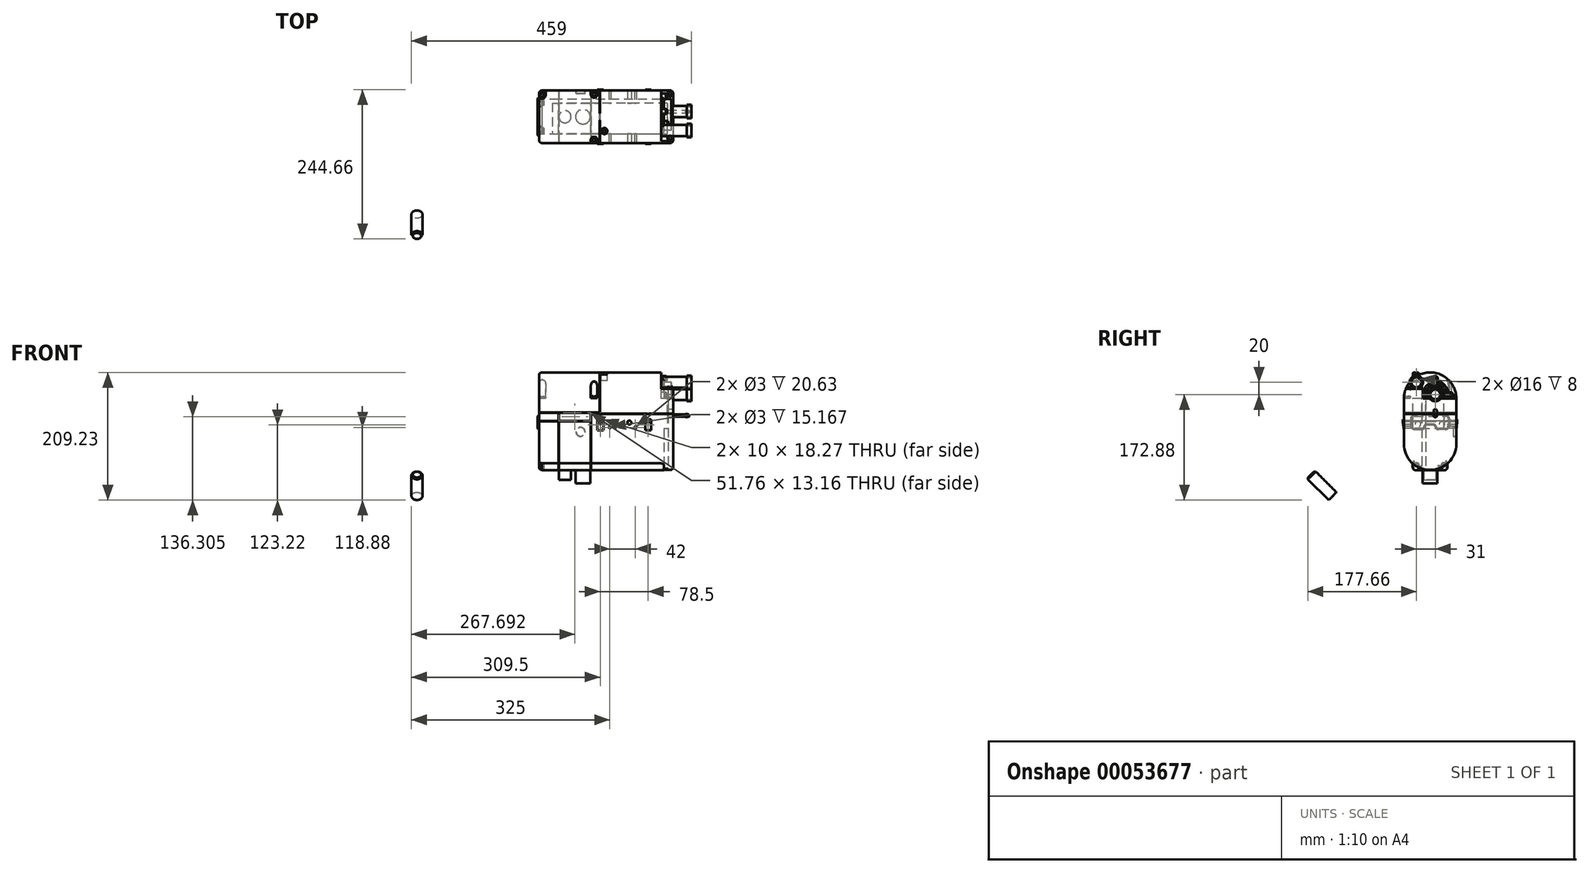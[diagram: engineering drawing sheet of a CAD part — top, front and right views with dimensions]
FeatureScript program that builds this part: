
annotation { "Feature Type Name" : "Feature", "Feature Type Description" : "" }
export const myFeature = defineFeature(function(context is Context, id is Id, definition is map)
    precondition{}
    {
        {
            var Q0;
            Q0=qCreatedBy(makeId("Front.planeOp"),FACE);
            var sketch = newSketch(context, id + "F0", { "sketchPlane" : qUnion([Q0])});
            skLineSegment(sketch, "E0.bottom", {"start": v(0, 160) * mm, "end": v(220, 160) * mm});
            skLineSegment(sketch, "E0.top", {"start": v(0, 0) * mm, "end": v(220, 0) * mm});
            skLineSegment(sketch, "E0.left", {"start": v(0, 160) * mm, "end": v(0, 0) * mm});
            skLineSegment(sketch, "E0.right", {"start": v(220, 160) * mm, "end": v(220, 0) * mm});
            skLineSegment(sketch, "E1", {"start": v(220, 144) * mm, "end": v(255.31, 144) * mm, "construction": true});
            skLineSegment(sketch, "E2", {"start": v(220, 124) * mm, "end": v(252.52, 124) * mm, "construction": true});
            skLineSegment(sketch, "E3", {"start": v(199, 133.89) * mm, "end": v(199, 118.06) * mm});
            skLineSegment(sketch, "E4", {"start": v(236.23, 153) * mm, "end": v(236.23, 135) * mm, "construction": true});
            skLineSegment(sketch, "E5", {"start": v(123.03, 118) * mm, "end": v(43.7, 118) * mm});
            skLineSegment(sketch, "E6", {"start": v(5, 154.65) * mm, "end": v(5, 139.81) * mm});
            skLineSegment(sketch, "E7", {"start": v(205, 0) * mm, "end": v(205, 15.7) * mm});
            skLineSegment(sketch, "E8", {"start": v(43, 3.14) * mm, "end": v(43, -20.65) * mm});
            skLineSegment(sketch, "E9", {"start": v(72, 4.14) * mm, "end": v(72, -25) * mm});
            skLineSegment(sketch, "E10", {"start": v(33.26, -16) * mm, "end": v(52.94, -16) * mm});
            skLineSegment(sketch, "E11", {"start": v(59.34, -20) * mm, "end": v(83.9, -20) * mm});
            skLineSegment(sketch, "E12", {"start": v(220, 92.5) * mm, "end": v(85.03, 92.5) * mm});
            skLineSegment(sketch, "E13", {"start": v(246, 91.62) * mm, "end": v(246, 86.96) * mm});
            skLineSegment(sketch, "E14", {"start": v(217, 89) * mm, "end": v(251.41, 89) * mm});
            skLineSegment(sketch, "E15.bottom", {"start": v(243.5, 92.15) * mm, "end": v(240.5, 92.15) * mm});
            skLineSegment(sketch, "E15.top", {"start": v(243.5, 86.65) * mm, "end": v(240.5, 86.65) * mm});
            skLineSegment(sketch, "E15.left", {"start": v(243.5, 92.15) * mm, "end": v(243.5, 86.65) * mm});
            skLineSegment(sketch, "E15.right", {"start": v(240.5, 92.15) * mm, "end": v(240.5, 86.65) * mm});
            skLineSegment(sketch, "E16", {"start": v(101.2, 157) * mm, "end": v(111.86, 157) * mm});
            skLineSegment(sketch, "E17", {"start": v(-1.72, 87.54) * mm, "end": v(-1.72, 71.83) * mm});
            skLineSegment(sketch, "E18", {"start": v(206.56, 127.25) * mm, "end": v(206.56, 120.25) * mm});
            skLineSegment(sketch, "E19", {"start": v(206.56, 123.75) * mm, "end": v(208.56, 123.75) * mm});
            skLineSegment(sketch, "E20", {"start": v(89.7, 118) * mm, "end": v(89.7, 120.5) * mm});
            skSolve(sketch);
        }
        {
            var Q0;
            Q0=qCreatedBy(makeId("Right.planeOp"),FACE);
            var sketch = newSketch(context, id + "F1", { "sketchPlane" : qUnion([Q0])});
            skArc(sketch, "E21", {"start": v(86, 117.35) * mm, "mid": v(43, 160.35) * mm, "end": v(0, 117.35) * mm});
            skArc(sketch, "E22", {"start": v(0, 43.35) * mm, "mid": v(43, 0.35) * mm, "end": v(86, 43.35) * mm});
            skLineSegment(sketch, "E23", {"start": v(0, 117.35) * mm, "end": v(0, 43.35) * mm});
            skLineSegment(sketch, "E24", {"start": v(86, 117.35) * mm, "end": v(86, 43.35) * mm});
            skLineSegment(sketch, "E25", {"start": v(0, 83.29) * mm, "end": v(-2.3, 83.29) * mm, "construction": true});
            skLineSegment(sketch, "E26", {"start": v(86, 83.29) * mm, "end": v(87.7, 83.29) * mm, "construction": true});
            skSolve(sketch);
        }
        {
            var Q0;
            Q0=qCreatedBy(makeId("Top.planeOp"),FACE);
            var sketch = newSketch(context, id + "F2", { "sketchPlane" : qUnion([Q0])});
            skLineSegment(sketch, "E27", {"start": v(-0.36, 86) * mm, "end": v(219.64, 86) * mm});
            skLineSegment(sketch, "E28", {"start": v(-0.36, 0) * mm, "end": v(219.64, 0) * mm});
            skLineSegment(sketch, "E29", {"start": v(-0.36, 86) * mm, "end": v(-0.36, 0) * mm});
            skLineSegment(sketch, "E30", {"start": v(221.58, 20.5) * mm, "end": v(257.3, 20.5) * mm});
            skLineSegment(sketch, "E31", {"start": v(222.14, 51.5) * mm, "end": v(259.8, 51.5) * mm});
            skLineSegment(sketch, "E32", {"start": v(219.64, 86) * mm, "end": v(219.64, 0) * mm});
            skLineSegment(sketch, "E33", {"start": v(199.64, 81.83) * mm, "end": v(199.64, 54.29) * mm});
            skLineSegment(sketch, "E34", {"start": v(199.64, 75.94) * mm, "end": v(204.64, 75.94) * mm});
            skLineSegment(sketch, "E35", {"start": v(204.64, 75.94) * mm, "end": v(204.64, 27.94) * mm});
            skLineSegment(sketch, "E36", {"start": v(204.64, 27.94) * mm, "end": v(199.48, 27.94) * mm});
            skLineSegment(sketch, "E37", {"start": v(204.64, 74.7) * mm, "end": v(216.64, 74.7) * mm});
            skLineSegment(sketch, "E38", {"start": v(216.64, 74.7) * mm, "end": v(216.64, 29.7) * mm});
            skLineSegment(sketch, "E39", {"start": v(216.64, 29.7) * mm, "end": v(204.64, 29.7) * mm});
            skLineSegment(sketch, "E40", {"start": v(216.64, 67.02) * mm, "end": v(218.64, 67.02) * mm});
            skLineSegment(sketch, "E41", {"start": v(218.64, 67.02) * mm, "end": v(218.64, 34.02) * mm});
            skLineSegment(sketch, "E42", {"start": v(218.64, 34.02) * mm, "end": v(216.64, 34.02) * mm});
            skLineSegment(sketch, "E43", {"start": v(185.57, 86) * mm, "end": v(185.57, 87.56) * mm});
            skLineSegment(sketch, "E44", {"start": v(185.57, 87.56) * mm, "end": v(175.64, 87.56) * mm});
            skLineSegment(sketch, "E45", {"start": v(175.64, 87.56) * mm, "end": v(175.64, 86) * mm});
            skLineSegment(sketch, "E46", {"start": v(105.14, 86) * mm, "end": v(105.14, 87.5) * mm});
            skLineSegment(sketch, "E47", {"start": v(95.14, 86) * mm, "end": v(95.14, 87.5) * mm});
            skLineSegment(sketch, "E48", {"start": v(95.14, 87.5) * mm, "end": v(105.14, 87.5) * mm});
            skLineSegment(sketch, "E49", {"start": v(207.64, 74.7) * mm, "end": v(207.64, 82.59) * mm});
            skLineSegment(sketch, "E50", {"start": v(207.64, 82.59) * mm, "end": v(199.7, 82.59) * mm});
            skLineSegment(sketch, "E51", {"start": v(201.63, 54.6) * mm, "end": v(207.36, 54.6) * mm});
            skLineSegment(sketch, "E52", {"start": v(201.82, 46.6) * mm, "end": v(207.17, 46.6) * mm});
            skSolve(sketch);
        }
        {
            var Q0;
            Q0 = qSketchRegion(id + "F1", true);
            extrude(context, id + "F3", {"entities" : qUnion([Q0]), "depth" : 220 * mm});
        }
        {
            var Q0;
            Q0=makeQuery(id+"F3.opExtrude","CAP_FACE",FACE,{"disambiguationData":[OSD([sQuery(id+"F1.wireOp",EDGE,"E21"),sQuery(id+"F1.wireOp",EDGE,"E22"),sQuery(id+"F1.wireOp",EDGE,"E23"),sQuery(id+"F1.wireOp",EDGE,"E24")])],"isStart":false});
            var sketch = newSketch(context, id + "F4", { "sketchPlane" : qUnion([Q0])});
            skPoint(sketch, "E53.orphan", {"position": v(86, 117.35) * mm});
            skLineSegment(sketch, "E54", {"start": v(86, 117.35) * mm, "end": v(31.1, 117.35) * mm});
            skLineSegment(sketch, "E55", {"start": v(31.1, 117.35) * mm, "end": v(31.1, 133.35) * mm});
            skLineSegment(sketch, "E56", {"start": v(31.1, 133.35) * mm, "end": v(3.09, 133.35) * mm});
            skArc(sketch, "E57.0", {"start": v(86, 117.35) * mm, "mid": v(51.15, 159.57) * mm, "end": v(3.09, 133.35) * mm});
            skPoint(sketch, "E58.orphan", {"position": v(0, 117.35) * mm});
            skSolve(sketch);
        }
        {
            var Q0;
            Q0 = qSketchRegion(id + "F4", true);
            extrude(context, id + "F5", {"entities" : qUnion([Q0]), "operationType" : NewBodyOperationType.REMOVE, "oppositeDirection" : true, "depth" : 20 * mm});
        }
        {
            var Q0;
            Q0=makeQuery(id+"F5.boolean.opBoolean","COPY",FACE,{"derivedFrom":makeQuery(id+"F5.opExtrude","CAP_FACE",FACE,{"disambiguationData":[OSD([sQuery(id+"F4.wireOp",EDGE,"E54"),sQuery(id+"F4.wireOp",EDGE,"E55"),sQuery(id+"F4.wireOp",EDGE,"E56"),sQuery(id+"F4.wireOp",EDGE,"E57.0")])],"isStart":false})});
            var sketch = newSketch(context, id + "F6", { "sketchPlane" : qUnion([Q0])});
            skCircle(sketch, "E59", {"center": v(51.5, 124) * mm, "radius": 9 * mm});
            skCircle(sketch, "E60", {"center": v(20.5, 144) * mm, "radius": 9 * mm});
            skSolve(sketch);
        }
        {
            var Q0;
            Q0 = qSketchRegion(id + "F6", true);
            extrude(context, id + "F7", {"entities" : qUnion([Q0]), "operationType" : NewBodyOperationType.ADD, "depth" : 50 * mm});
        }
        {
            var Q0;
            Q0=makeQuery(id+"F7.opExtrude","CAP_FACE",FACE,{"disambiguationData":[OSD([sQuery(id+"F6.wireOp",EDGE,"E60")])],"isStart":false});
            var sketch = newSketch(context, id + "F8", { "sketchPlane" : qUnion([Q0])});
            skCircle(sketch, "E61", {"center": v(20.5, 144) * mm, "radius": 11 * mm});
            skCircle(sketch, "E62.0", {"center": v(51.5, 124) * mm, "radius": 9 * mm, "construction": true});
            skCircle(sketch, "E63", {"center": v(51.5, 124) * mm, "radius": 11 * mm});
            skCircle(sketch, "E64", {"center": v(20.5, 144) * mm, "radius": 8 * mm});
            skCircle(sketch, "E65", {"center": v(51.5, 124) * mm, "radius": 8 * mm});
            skSolve(sketch);
        }
        {
            var Q0;
            Q0 = qSketchRegion(id + "F8", true);
            extrude(context, id + "F9", {"entities" : qUnion([Q0]), "operationType" : NewBodyOperationType.ADD, "oppositeDirection" : true, "depth" : 8 * mm});
        }
        {
            var Q0;
            Q0=makeQuery(id+"F9.boolean.opBoolean","MERGE",FACE,{"derivedFrom":[makeQuery(id+"F7.opExtrude","CAP_FACE",FACE,{"disambiguationData":[OSD([sQuery(id+"F6.wireOp",EDGE,"E60")])],"isStart":false}),makeQuery(id+"F9.opExtrude","CAP_FACE",FACE,{"disambiguationData":[OSD([sQuery(id+"F8.wireOp",EDGE,"E61"),sQuery(id+"F8.wireOp",EDGE,"E64")])],"isStart":true})]});
            var sketch = newSketch(context, id + "F10", { "sketchPlane" : qUnion([Q0])});
            skCircle(sketch, "E66", {"center": v(20.5, 144) * mm, "radius": 8 * mm});
            skCircle(sketch, "E67.0", {"center": v(51.5, 124) * mm, "radius": 11 * mm, "construction": true});
            skCircle(sketch, "E68", {"center": v(51.5, 124) * mm, "radius": 8 * mm});
            skSolve(sketch);
        }
        {
            var Q0;
            Q0 = qSketchRegion(id + "F10", true);
            extrude(context, id + "F11", {"entities" : qUnion([Q0]), "operationType" : NewBodyOperationType.REMOVE, "oppositeDirection" : true, "depth" : 8 * mm});
        }
        {
            var Q0;
            Q0=makeQuery(id+"F5.boolean.opBoolean","COPY",FACE,{"derivedFrom":makeQuery(id+"F5.opExtrude","CAP_FACE",FACE,{"disambiguationData":[OSD([sQuery(id+"F4.wireOp",EDGE,"E54"),sQuery(id+"F4.wireOp",EDGE,"E55"),sQuery(id+"F4.wireOp",EDGE,"E56"),sQuery(id+"F4.wireOp",EDGE,"E57.0")])],"isStart":false})});
            var sketch = newSketch(context, id + "F12", { "sketchPlane" : qUnion([Q0])});
            skLineSegment(sketch, "E69", {"start": v(27.41, 149.76) * mm, "end": v(43, 149.76) * mm});
            skArc(sketch, "E70", {"start": v(43, 149.76) * mm, "mid": v(65.92, 140.27) * mm, "end": v(75.41, 117.35) * mm});
            skLineSegment(sketch, "E71.0", {"start": v(86, 117.35) * mm, "end": v(57.56, 117.35) * mm});
            skLineSegment(sketch, "E72.0", {"start": v(31.1, 117.35) * mm, "end": v(31.1, 133.35) * mm});
            skLineSegment(sketch, "E73.0", {"start": v(31.1, 133.35) * mm, "end": v(20.5, 133.35) * mm});
            skLineSegment(sketch, "E74", {"start": v(20.5, 144) * mm, "end": v(20.5, 133.35) * mm});
            skLineSegment(sketch, "E75", {"start": v(31.1, 117.35) * mm, "end": v(57.56, 117.35) * mm});
            skPoint(sketch, "E76.orphan", {"position": v(3.09, 133.35) * mm});
            skLineSegment(sketch, "E77", {"start": v(27.41, 149.76) * mm, "end": v(20.5, 144) * mm});
            skSolve(sketch);
        }
        {
            var Q0;
            {var subQ1=sQuery(id+"F12.wireOp",EDGE,"E69");Q0=makeQuery(id+"F12.imprint","IMPRINT",FACE,{"disambiguationData":[TD([[makeQuery(id+"F12.imprint","IMPRINT",EDGE,{"derivedFrom":subQ1}),-1.0]])]});}
            extrude(context, id + "F13", {"entities" : qUnion([Q0]), "operationType" : NewBodyOperationType.ADD, "depth" : 5 * mm});
        }
        {
            var Q0;
            Q0=makeQuery(id+"F13.opExtrude","CAP_FACE",FACE,{"disambiguationData":[OSD([sQuery(id+"F6.wireOp",EDGE,"E59"),sQuery(id+"F6.wireOp",EDGE,"E60"),sQuery(id+"F12.wireOp",EDGE,"E69"),sQuery(id+"F12.wireOp",EDGE,"E70"),sQuery(id+"F12.wireOp",EDGE,"E71.0"),sQuery(id+"F12.wireOp",EDGE,"E72.0"),sQuery(id+"F12.wireOp",EDGE,"E73.0"),sQuery(id+"F12.wireOp",EDGE,"E74"),sQuery(id+"F12.wireOp",EDGE,"E75")])],"isStart":false});
            var sketch = newSketch(context, id + "F14", { "sketchPlane" : qUnion([Q0])});
            skLineSegment(sketch, "E78", {"start": v(31.1, 117.35) * mm, "end": v(31.1, 124) * mm});
            skLineSegment(sketch, "E79", {"start": v(71.9, 117.35) * mm, "end": v(71.9, 124) * mm});
            skArc(sketch, "E80", {"start": v(71.9, 124) * mm, "mid": v(51.5, 144.4) * mm, "end": v(31.1, 124) * mm});
            skLineSegment(sketch, "E81", {"start": v(31.1, 117.35) * mm, "end": v(71.9, 117.35) * mm});
            skArc(sketch, "E82.0", {"start": v(20.5, 135) * mm, "mid": v(26.86, 137.64) * mm, "end": v(29.5, 144) * mm});
            skLineSegment(sketch, "E83", {"start": v(29.5, 144) * mm, "end": v(29.5, 133.35) * mm});
            skPoint(sketch, "E84.orphan", {"position": v(27.41, 149.76) * mm});
            skLineSegment(sketch, "E85", {"start": v(20.5, 133.35) * mm, "end": v(29.5, 133.35) * mm});
            skLineSegment(sketch, "E86", {"start": v(20.5, 135) * mm, "end": v(20.5, 133.35) * mm});
            skPoint(sketch, "E87.orphan", {"position": v(3.09, 133.35) * mm});
            skPoint(sketch, "E88.0.end.orphan", {"position": v(20.5, 135) * mm});
            skPoint(sketch, "E88.0.start.orphan", {"position": v(12.11, 147.26) * mm});
            skSolve(sketch);
        }
        {
            var Q0;
            Q0 = qSketchRegion(id + "F14", true);
            extrude(context, id + "F15", {"entities" : qUnion([Q0]), "operationType" : NewBodyOperationType.ADD, "depth" : 12 * mm});
        }
        {
            var Q0;
            Q0=makeQuery(id+"F15.opExtrude","CAP_FACE",FACE,{"disambiguationData":[OSD([sQuery(id+"F14.wireOp",EDGE,"E78"),sQuery(id+"F14.wireOp",EDGE,"E79"),sQuery(id+"F14.wireOp",EDGE,"E80"),sQuery(id+"F14.wireOp",EDGE,"E81")])],"isStart":false});
            var sketch = newSketch(context, id + "F16", { "sketchPlane" : qUnion([Q0])});
            skLineSegment(sketch, "E89", {"start": v(35, 117.35) * mm, "end": v(35, 124) * mm});
            skLineSegment(sketch, "E90", {"start": v(68, 117.35) * mm, "end": v(68, 124) * mm});
            skArc(sketch, "E91", {"start": v(68, 124) * mm, "mid": v(51.5, 140.5) * mm, "end": v(35, 124) * mm});
            skLineSegment(sketch, "E92", {"start": v(35, 117.35) * mm, "end": v(68, 117.35) * mm});
            skSolve(sketch);
        }
        {
            var Q0;
            Q0 = qSketchRegion(id + "F16", true);
            extrude(context, id + "F17", {"entities" : qUnion([Q0]), "operationType" : NewBodyOperationType.ADD, "depth" : 2 * mm});
        }
        {
            var Q0;
            Q0=qCreatedBy(makeId("Top.planeOp"),FACE);
            cPlane(context, id + "F18", {"entities" : qUnion([Q0]), "cplaneType" : CPlaneType.OFFSET, "offset" : 118 * mm, "width" : 150 * mm, "height" : 150 * mm});
        }
        {
            var Q0;
            Q0=qCreatedBy(id+"F18.planeOp",FACE);
            var sketch = newSketch(context, id + "F19", { "sketchPlane" : qUnion([Q0])});
            skLineSegment(sketch, "E93", {"start": v(0, 72.78) * mm, "end": v(5.07, 72.78) * mm});
            skLineSegment(sketch, "E94", {"start": v(10.79, 85.9) * mm, "end": v(10.79, 77.81) * mm});
            skLineSegment(sketch, "E95.0", {"start": v(-0.36, 86) * mm, "end": v(-0.36, 0) * mm, "construction": true});
            skLineSegment(sketch, "E95.1", {"start": v(-0.36, 86) * mm, "end": v(219.64, 86) * mm, "construction": true});
            skLineSegment(sketch, "E95.2", {"start": v(-0.36, 0) * mm, "end": v(219.64, 0) * mm, "construction": true});
            skLineSegment(sketch, "E96", {"start": v(84.87, 86) * mm, "end": v(84.87, 79.73) * mm});
            skLineSegment(sketch, "E97", {"start": v(95.62, 86) * mm, "end": v(95.62, 79.73) * mm});
            skLineSegment(sketch, "E98", {"start": v(84.82, 0) * mm, "end": v(84.82, 4.9) * mm});
            skLineSegment(sketch, "E99", {"start": v(95.57, 0) * mm, "end": v(95.57, 4.9) * mm});
            skArc(sketch, "E100", {"start": v(84.87, 79.73) * mm, "mid": v(90.25, 74.36) * mm, "end": v(95.62, 79.73) * mm});
            skArc(sketch, "E101", {"start": v(95.57, 4.9) * mm, "mid": v(90.2, 10.28) * mm, "end": v(84.82, 4.9) * mm});
            skArc(sketch, "E102", {"start": v(5.07, 72.78) * mm, "mid": v(8.88, 74.22) * mm, "end": v(10.79, 77.81) * mm});
            skLineSegment(sketch, "E103", {"start": v(0, 72.78) * mm, "end": v(-0.36, 86) * mm});
            skLineSegment(sketch, "E104", {"start": v(10.79, 85.9) * mm, "end": v(-0.36, 86) * mm, "construction": true});
            skLineSegment(sketch, "E105", {"start": v(84.87, 86) * mm, "end": v(95.62, 86) * mm});
            skLineSegment(sketch, "E106", {"start": v(84.82, 0) * mm, "end": v(95.57, 0) * mm});
            skLineSegment(sketch, "E107", {"start": v(10.79, 85.9) * mm, "end": v(10.79, 88.78) * mm});
            skLineSegment(sketch, "E108", {"start": v(10.79, 88.78) * mm, "end": v(-0.36, 88.78) * mm});
            skLineSegment(sketch, "E109", {"start": v(-0.36, 88.78) * mm, "end": v(-0.36, 86) * mm});
            skSolve(sketch);
        }
        {
            var Q0;
            Q0 = qSketchRegion(id + "F19", true);
            extrude(context, id + "F20", {"entities" : qUnion([Q0]), "operationType" : NewBodyOperationType.REMOVE, "endBound" : BoundingType.THROUGH_ALL, "depth" : 25 * mm});
        }
        {
            var Q0;
            Q0=makeQuery(id+"F17.opExtrude","CAP_EDGE",EDGE,{"disambiguationData":[OSD([sQuery(id+"F16.wireOp",EDGE,"E91")])],"isStart":false});
            chamfer(context, id + "F21", {"entities" : qUnion([Q0]), "width" : 2 * mm, "tangentPropagation" : true});
        }
        {
            var Q0;
            Q0=makeQuery(id+"F1.imprint","IMPRINT",FACE,{"disambiguationData":[TD([[makeQuery(id+"F1.imprint","IMPRINT",EDGE,{"derivedFrom":sQuery(id+"F1.wireOp",EDGE,"E21")}),1.0]])]});
            var sketch = newSketch(context, id + "F22", { "sketchPlane" : qUnion([Q0])});
            skArc(sketch, "E110.0", {"start": v(14.5, 11.15) * mm, "mid": v(43, 0.35) * mm, "end": v(71.5, 11.15) * mm});
            skLineSegment(sketch, "E111", {"start": v(71.5, 11.15) * mm, "end": v(71.5, 5) * mm});
            skArc(sketch, "E112", {"start": v(66.5, 0) * mm, "mid": v(70.04, 1.46) * mm, "end": v(71.5, 5) * mm});
            skLineSegment(sketch, "E113", {"start": v(66.5, 0) * mm, "end": v(19.5, 0) * mm});
            skLineSegment(sketch, "E114", {"start": v(14.5, 11.15) * mm, "end": v(14.5, 5) * mm});
            skArc(sketch, "E115", {"start": v(14.5, 5) * mm, "mid": v(15.96, 1.46) * mm, "end": v(19.5, 0) * mm});
            skPoint(sketch, "E116.orphan", {"position": v(86, 43.35) * mm});
            skPoint(sketch, "E117.orphan", {"position": v(0, 43.35) * mm});
            skSolve(sketch);
        }
        {
            var Q0;
            Q0 = qSketchRegion(id + "F22", true);
            extrude(context, id + "F23", {"entities" : qUnion([Q0]), "operationType" : NewBodyOperationType.ADD, "depth" : 205 * mm});
        }
        {
            var Q0;
            Q0=makeQuery(id+"F23.boolean.opBoolean","MERGE",FACE,{"derivedFrom":[makeQuery(id+"F3.opExtrude","CAP_FACE",FACE,{"disambiguationData":[OSD([sQuery(id+"F1.wireOp",EDGE,"E21"),sQuery(id+"F1.wireOp",EDGE,"E22"),sQuery(id+"F1.wireOp",EDGE,"E23"),sQuery(id+"F1.wireOp",EDGE,"E24")])],"isStart":true}),makeQuery(id+"F23.opExtrude","CAP_FACE",FACE,{"disambiguationData":[OSD([sQuery(id+"F22.wireOp",EDGE,"E110.0"),sQuery(id+"F22.wireOp",EDGE,"E111"),sQuery(id+"F22.wireOp",EDGE,"E112"),sQuery(id+"F22.wireOp",EDGE,"E113"),sQuery(id+"F22.wireOp",EDGE,"E114"),sQuery(id+"F22.wireOp",EDGE,"E115")])],"isStart":true})]});
            var sketch = newSketch(context, id + "F24", { "sketchPlane" : qUnion([Q0])});
            skLineSegment(sketch, "E118", {"start": v(-43, 0) * mm, "end": v(-43, 20) * mm, "construction": true});
            skArc(sketch, "E119", {"start": v(-71.5, 11.15) * mm, "mid": v(-69.51, 10.4) * mm, "end": v(-67.52, 11.15) * mm});
            skArc(sketch, "E120", {"start": v(-61.01, 7.1) * mm, "mid": v(-62.76, 11.55) * mm, "end": v(-67.52, 11.15) * mm});
            skArc(sketch, "E121", {"start": v(-61.01, 7.1) * mm, "mid": v(-60.8, 4.98) * mm, "end": v(-59.25, 3.54) * mm});
            skPoint(sketch, "E122.orphan", {"position": v(-86, 43.35) * mm});
            skArc(sketch, "E123.MirrorCS", {"start": v(-14.5, 11.15) * mm, "mid": v(-16.49, 10.4) * mm, "end": v(-18.48, 11.15) * mm});
            skArc(sketch, "E124.MirrorCS", {"start": v(-24.99, 7.1) * mm, "mid": v(-23.24, 11.55) * mm, "end": v(-18.48, 11.15) * mm});
            skArc(sketch, "E125.MirrorCS", {"start": v(-24.99, 7.1) * mm, "mid": v(-25.2, 4.98) * mm, "end": v(-26.75, 3.54) * mm});
            skPoint(sketch, "E126.orphan", {"position": v(0, 43.35) * mm});
            skLineSegment(sketch, "E127.0", {"start": v(-71.5, 11.15) * mm, "end": v(-71.5, 5) * mm});
            skArc(sketch, "E128.0", {"start": v(-66.5, 0) * mm, "mid": v(-70.04, 1.46) * mm, "end": v(-71.5, 5) * mm});
            skLineSegment(sketch, "E129.0", {"start": v(-75.94, 0) * mm, "end": v(-27.94, 0) * mm});
            skLineSegment(sketch, "E130.0", {"start": v(-14.5, 11.15) * mm, "end": v(-14.5, 5) * mm});
            skArc(sketch, "E131.0", {"start": v(-14.5, 5) * mm, "mid": v(-15.96, 1.46) * mm, "end": v(-19.5, 0) * mm});
            skArc(sketch, "E132.trimOffspring", {"start": v(-26.75, 3.54) * mm, "mid": v(-43, 0.35) * mm, "end": v(-59.25, 3.54) * mm});
            skLineSegment(sketch, "E133", {"start": v(-27.94, 0) * mm, "end": v(-19.5, 0) * mm});
            skSolve(sketch);
        }
        {
            var Q0;
            Q0 = qSketchRegion(id + "F24", true);
            extrude(context, id + "F25", {"entities" : qUnion([Q0]), "operationType" : NewBodyOperationType.REMOVE, "oppositeDirection" : true, "depth" : 5 * mm});
        }
        {
            var Q0;
            Q0=makeQuery(id+"F2.imprint","IMPRINT",FACE,{"disambiguationData":[TD([[makeQuery(id+"F2.imprint","IMPRINT",EDGE,{"derivedFrom":sQuery(id+"F2.wireOp",EDGE,"E27")}),-1.0]])]});
            var sketch = newSketch(context, id + "F26", { "sketchPlane" : qUnion([Q0])});
            skCircle(sketch, "E134", {"center": v(42.64, 43) * mm, "radius": 10 * mm});
            skCircle(sketch, "E135", {"center": v(72, 43) * mm, "radius": 12 * mm});
            skSolve(sketch);
        }
        {
            var Q0;
            {var subQ0=sQuery(id+"F1.wireOp",EDGE,"E21");var subQ1=sQuery(id+"F1.wireOp",EDGE,"E23");Q0=makeQuery(id+"F20.boolean.opBoolean","SPLIT",EDGE,{"disambiguationData":[TD([makeQuery(id+"F3.opExtrude","SWEPT_FACE",FACE,{"disambiguationData":[OSD([subQ1])]})])],"derivedFrom":makeQuery(id+"F3.opExtrude","CAP_EDGE",EDGE,{"disambiguationData":[OSD([subQ0])],"isStart":true})});}
            var Q1;
            Q1=makeQuery(id+"F3.opExtrude","CAP_EDGE",EDGE,{"disambiguationData":[OSD([sQuery(id+"F1.wireOp",EDGE,"E24")])],"isStart":false});
            var Q2;
            {var subQ0=sQuery(id+"F4.wireOp",EDGE,"E54");var subQ1=sQuery(id+"F4.wireOp",EDGE,"E57.0");var subQ2=sQuery(id+"F6.wireOp",EDGE,"E60");Q2=makeQuery(id+"F7.boolean.opBoolean","SPLIT",EDGE,{"disambiguationData":[TD([makeQuery(id+"F3.opExtrude","SWEPT_FACE",FACE,{"disambiguationData":[OSD([sQuery(id+"F1.wireOp",EDGE,"E21")])]}),makeQuery(id+"F3.opExtrude","SWEPT_FACE",FACE,{"disambiguationData":[OSD([sQuery(id+"F1.wireOp",EDGE,"E24")])]}),makeQuery(id+"F5.boolean.opBoolean","COPY",FACE,{"derivedFrom":makeQuery(id+"F5.opExtrude","SWEPT_FACE",FACE,{"disambiguationData":[OSD([subQ0])]})}),makeQuery(id+"F5.boolean.opBoolean","COPY",FACE,{"derivedFrom":makeQuery(id+"F5.opExtrude","CAP_FACE",FACE,{"disambiguationData":[OSD([subQ0,sQuery(id+"F4.wireOp",EDGE,"E55"),sQuery(id+"F4.wireOp",EDGE,"E56"),subQ1])],"isStart":false})}),makeQuery(id+"F7.opExtrude","SWEPT_FACE",FACE,{"disambiguationData":[OSD([subQ2])]}),makeQuery(id+"F7.opExtrude","CAP_FACE",FACE,{"disambiguationData":[OSD([subQ2])],"isStart":true})])],"derivedFrom":makeQuery(id+"F5.boolean.opBoolean","COPY",EDGE,{"derivedFrom":makeQuery(id+"F5.opExtrude","CAP_EDGE",EDGE,{"disambiguationData":[OSD([subQ1])],"isStart":false})})});}
            fillet(context, id + "F27", {"entities" : qUnion([Q0, Q1, Q2]), "radius" : 5 * mm, "tangentPropagation" : true, "allowEdgeOverflow" : false});
        }
        {
            var Q0;
            Q0=makeQuery(id+"F13.opExtrude","CAP_EDGE",EDGE,{"disambiguationData":[OSD([sQuery(id+"F12.wireOp",EDGE,"E69")])],"isStart":false});
            fillet(context, id + "F28", {"entities" : qUnion([Q0]), "radius" : 3 * mm, "tangentPropagation" : true, "allowEdgeOverflow" : false});
        }
        {
            var Q0;
            Q0 = qSketchRegion(id + "F26", true);
            extrude(context, id + "F29", {"entities" : qUnion([Q0]), "operationType" : NewBodyOperationType.ADD, "oppositeDirection" : true, "depth" : 16 * mm});
        }
        {
            var Q0;
            Q0=makeQuery(id+"F29.opExtrude","CAP_FACE",FACE,{"disambiguationData":[OSD([sQuery(id+"F26.wireOp",EDGE,"E135")])],"isStart":false});
            var sketch = newSketch(context, id + "F30", { "sketchPlane" : qUnion([Q0])});
            skCircle(sketch, "E136.0", {"center": v(72, -43) * mm, "radius": 12 * mm});
            skSolve(sketch);
        }
        {
            var Q0;
            Q0 = qSketchRegion(id + "F30", true);
            extrude(context, id + "F31", {"entities" : qUnion([Q0]), "operationType" : NewBodyOperationType.ADD, "depth" : 5.5 * mm});
        }
        {
            var Q0;
            Q0=qCreatedBy(makeId("Front.planeOp"),FACE);
            var sketch = newSketch(context, id + "F32", { "sketchPlane" : qUnion([Q0])});
            skCircle(sketch, "E137", {"center": v(148, 78) * mm, "radius": 3.25 * mm});
            skCircle(sketch, "E138", {"center": v(158, 70) * mm, "radius": 1.5 * mm});
            skCircle(sketch, "E139", {"center": v(116, 70) * mm, "radius": 1.5 * mm});
            skSolve(sketch);
        }
        {
            var Q0;
            Q0 = qSketchRegion(id + "F32", true);
            extrude(context, id + "F33", {"entities" : qUnion([Q0]), "operationType" : NewBodyOperationType.REMOVE, "endBound" : BoundingType.THROUGH_ALL, "oppositeDirection" : true, "depth" : 25 * mm});
        }
        {
            var Q0;
            Q0=qCreatedBy(makeId("Right.planeOp"),FACE);
            cPlane(context, id + "F34", {"entities" : qUnion([Q0]), "cplaneType" : CPlaneType.OFFSET, "offset" : 95.5 * mm, "width" : 150 * mm, "height" : 150 * mm});
        }
        {
            var Q0;
            Q0=qCreatedBy(id+"F34.planeOp",FACE);
            var sketch = newSketch(context, id + "F35", { "sketchPlane" : qUnion([Q0])});
            skLineSegment(sketch, "E140", {"start": v(87.5, 83.48) * mm, "end": v(87.5, 78.98) * mm});
            skLineSegment(sketch, "E141", {"start": v(87.5, 78.98) * mm, "end": v(86, 65.2) * mm});
            skLineSegment(sketch, "E142.0", {"start": v(86, 83.48) * mm, "end": v(86, 65.2) * mm});
            skLineSegment(sketch, "E143", {"start": v(87.5, 83.48) * mm, "end": v(86, 83.48) * mm});
            skLineSegment(sketch, "E144.0", {"start": v(0, 83.48) * mm, "end": v(0, 65.2) * mm});
            skLineSegment(sketch, "E145", {"start": v(0, 83.48) * mm, "end": v(-1.5, 83.48) * mm});
            skLineSegment(sketch, "E146", {"start": v(-1.5, 83.48) * mm, "end": v(-1.5, 78.98) * mm});
            skLineSegment(sketch, "E147", {"start": v(-1.5, 78.98) * mm, "end": v(0, 65.2) * mm});
            skPoint(sketch, "E148.orphan", {"position": v(86, 117.35) * mm});
            skPoint(sketch, "E149.orphan", {"position": v(86, 43.35) * mm});
            skPoint(sketch, "E150.orphan", {"position": v(0, 43.35) * mm});
            skPoint(sketch, "E151.orphan", {"position": v(0, 117.35) * mm});
            skSolve(sketch);
        }
        {
            var Q0;
            Q0 = qSketchRegion(id + "F35", true);
            extrude(context, id + "F36", {"entities" : qUnion([Q0]), "operationType" : NewBodyOperationType.ADD, "depth" : 10 * mm});
        }
        {
            var Q0;
            Q0=qCreatedBy(makeId("Right.planeOp"),FACE);
            cPlane(context, id + "F37", {"entities" : qUnion([Q0]), "cplaneType" : CPlaneType.OFFSET, "offset" : 174 * mm, "width" : 150 * mm, "height" : 150 * mm});
        }
        {
            var Q0;
            Q0=qCreatedBy(id+"F37.planeOp",FACE);
            var sketch = newSketch(context, id + "F38", { "sketchPlane" : qUnion([Q0])});
            skLineSegment(sketch, "E152.0", {"start": v(0, 83.48) * mm, "end": v(-1.5, 83.48) * mm});
            skLineSegment(sketch, "E152.1", {"start": v(0, 83.48) * mm, "end": v(0, 65.2) * mm});
            skLineSegment(sketch, "E152.2", {"start": v(-1.5, 83.48) * mm, "end": v(-1.5, 78.98) * mm});
            skLineSegment(sketch, "E152.3", {"start": v(-1.5, 78.98) * mm, "end": v(0, 65.2) * mm});
            skLineSegment(sketch, "E152.4", {"start": v(86, 83.48) * mm, "end": v(86, 65.2) * mm});
            skLineSegment(sketch, "E152.5", {"start": v(87.5, 83.48) * mm, "end": v(87.5, 78.98) * mm});
            skLineSegment(sketch, "E152.6", {"start": v(87.5, 78.98) * mm, "end": v(86, 65.2) * mm});
            skLineSegment(sketch, "E152.7", {"start": v(87.5, 83.48) * mm, "end": v(86, 83.48) * mm});
            skPoint(sketch, "E153.orphan", {"position": v(0, 117.35) * mm});
            skPoint(sketch, "E154.orphan", {"position": v(0, 43.35) * mm});
            skPoint(sketch, "E155.orphan", {"position": v(86, 117.35) * mm});
            skPoint(sketch, "E156.orphan", {"position": v(86, 43.35) * mm});
            skSolve(sketch);
        }
        {
            var Q0;
            Q0 = qSketchRegion(id + "F38", true);
            extrude(context, id + "F39", {"entities" : qUnion([Q0]), "operationType" : NewBodyOperationType.ADD, "depth" : 10 * mm});
        }
        {
            var Q0;
            Q0=makeQuery(id+"F1.imprint","IMPRINT",FACE,{"disambiguationData":[TD([[makeQuery(id+"F1.imprint","IMPRINT",EDGE,{"derivedFrom":sQuery(id+"F1.wireOp",EDGE,"E21")}),1.0]])]});
            var sketch = newSketch(context, id + "F40", { "sketchPlane" : qUnion([Q0])});
            skLineSegment(sketch, "E157", {"start": v(74.96, 83.9) * mm, "end": v(74.96, 73.67) * mm});
            skArc(sketch, "E158", {"start": v(67.76, 66.47) * mm, "mid": v(72.85, 68.58) * mm, "end": v(74.96, 73.67) * mm});
            skLineSegment(sketch, "E159", {"start": v(67.76, 66.47) * mm, "end": v(56.59, 66.47) * mm});
            skArc(sketch, "E160", {"start": v(51.36, 70.92) * mm, "mid": v(53.16, 67.73) * mm, "end": v(56.59, 66.47) * mm});
            skArc(sketch, "E161", {"start": v(51.36, 70.92) * mm, "mid": v(50.37, 72.68) * mm, "end": v(48.47, 73.37) * mm});
            skLineSegment(sketch, "E162", {"start": v(48.47, 73.37) * mm, "end": v(37.32, 73.37) * mm});
            skLineSegment(sketch, "E163", {"start": v(42.9, 73.37) * mm, "end": v(42.9, 94.44) * mm, "construction": true});
            skArc(sketch, "E164", {"start": v(74.96, 83.9) * mm, "mid": v(73.1, 88.38) * mm, "end": v(68.63, 90.24) * mm});
            skLineSegment(sketch, "E165", {"start": v(68.63, 90.24) * mm, "end": v(17.16, 90.24) * mm});
            skCircle(sketch, "E166", {"center": v(62.57, 75.72) * mm, "radius": 4.47 * mm});
            skArc(sketch, "E167.MirrorCS", {"start": v(34.43, 70.92) * mm, "mid": v(32.64, 67.73) * mm, "end": v(29.2, 66.47) * mm});
            skCircle(sketch, "E168.MirrorC", {"center": v(23.22, 75.72) * mm, "radius": 4.47 * mm});
            skLineSegment(sketch, "E169.MirrorCS", {"start": v(10.83, 83.9) * mm, "end": v(10.83, 73.67) * mm});
            skLineSegment(sketch, "E170.MirrorCS", {"start": v(18.03, 66.47) * mm, "end": v(29.2, 66.47) * mm});
            skArc(sketch, "E171.MirrorCS", {"start": v(18.03, 66.47) * mm, "mid": v(12.94, 68.58) * mm, "end": v(10.83, 73.67) * mm});
            skArc(sketch, "E172.MirrorCS", {"start": v(34.43, 70.92) * mm, "mid": v(35.42, 72.68) * mm, "end": v(37.32, 73.37) * mm});
            skArc(sketch, "E173.MirrorCS", {"start": v(10.83, 83.9) * mm, "mid": v(12.68, 88.38) * mm, "end": v(17.16, 90.24) * mm});
            skLineSegment(sketch, "E174", {"start": v(46.57, 87.47) * mm, "end": v(63.83, 87.47) * mm, "construction": true});
            skSolve(sketch);
        }
        {
            var Q0;
            Q0 = qSketchRegion(id + "F40", true);
            extrude(context, id + "F41", {"entities" : qUnion([Q0]), "operationType" : NewBodyOperationType.ADD, "oppositeDirection" : true, "depth" : 2 * mm});
        }
        {
            var Q0;
            Q0=makeQuery(id+"F41.opExtrude","CAP_EDGE",EDGE,{"disambiguationData":[OSD([sQuery(id+"F40.wireOp",EDGE,"E165")])],"isStart":false});
            chamfer(context, id + "F42", {"entities" : qUnion([Q0]), "width" : 2 * mm, "tangentPropagation" : true});
        }
        {
            var Q0;
            {var subQ1=sQuery(id+"F4.wireOp",EDGE,"E54");Q0=makeQuery(id+"F13.boolean.opBoolean","SPLIT",FACE,{"disambiguationData":[TD([makeQuery(id+"F3.opExtrude","SWEPT_FACE",FACE,{"disambiguationData":[OSD([sQuery(id+"F1.wireOp",EDGE,"E24")])]})])],"derivedFrom":makeQuery(id+"F5.boolean.opBoolean","COPY",FACE,{"derivedFrom":makeQuery(id+"F5.opExtrude","CAP_FACE",FACE,{"disambiguationData":[OSD([subQ1,sQuery(id+"F4.wireOp",EDGE,"E55"),sQuery(id+"F4.wireOp",EDGE,"E56"),sQuery(id+"F4.wireOp",EDGE,"E57.0")])],"isStart":false})})});}
            var sketch = newSketch(context, id + "F43", { "sketchPlane" : qUnion([Q0])});
            skArc(sketch, "E175.0", {"start": v(71.9, 124) * mm, "mid": v(71.83, 125.68) * mm, "end": v(71.63, 127.35) * mm});
            skLineSegment(sketch, "E176.0", {"start": v(81, 117.35) * mm, "end": v(71.9, 117.35) * mm});
            skLineSegment(sketch, "E177", {"start": v(47.5, 144) * mm, "end": v(47.5, 150.27) * mm});
            skLineSegment(sketch, "E178", {"start": v(55.5, 144) * mm, "end": v(55.5, 150.27) * mm});
            skArc(sketch, "E179", {"start": v(55.5, 150.27) * mm, "mid": v(51.5, 154.27) * mm, "end": v(47.5, 150.27) * mm});
            skArc(sketch, "E180.0", {"start": v(81, 117.35) * mm, "mid": v(62.9, 149.72) * mm, "end": v(25.84, 151.25) * mm, "construction": true});
            skLineSegment(sketch, "E181", {"start": v(81, 117.35) * mm, "end": v(81, 123.35) * mm});
            skArc(sketch, "E182", {"start": v(81, 123.35) * mm, "mid": v(79.83, 126.17) * mm, "end": v(77, 127.35) * mm});
            skLineSegment(sketch, "E183", {"start": v(77, 127.35) * mm, "end": v(71.63, 127.35) * mm});
            skPoint(sketch, "E184.orphan", {"position": v(31.1, 124) * mm});
            skArc(sketch, "E185.trimOffspring", {"start": v(55.5, 144) * mm, "mid": v(51.5, 144.4) * mm, "end": v(47.5, 144) * mm});
            skLineSegment(sketch, "E186", {"start": v(71.9, 124) * mm, "end": v(71.9, 117.35) * mm});
            skPoint(sketch, "E187.orphan", {"position": v(57.56, 117.35) * mm});
            skSolve(sketch);
        }
        {
            var Q0;
            Q0 = qSketchRegion(id + "F43", true);
            extrude(context, id + "F44", {"entities" : qUnion([Q0]), "operationType" : NewBodyOperationType.ADD, "depth" : 8 * mm});
        }
        {
            var Q0;
            Q0=qCreatedBy(makeId("Front.planeOp"),FACE);
            var sketch = newSketch(context, id + "F45", { "sketchPlane" : qUnion([Q0])});
            skLineSegment(sketch, "E188.0", {"start": v(220, 92.58) * mm, "end": v(220, 92.08) * mm});
            skLineSegment(sketch, "E189.0", {"start": v(0, 94.5) * mm, "end": v(0, 94) * mm});
            skLineSegment(sketch, "E190.0", {"start": v(99.25, 160) * mm, "end": v(99.75, 160) * mm});
            skLineSegment(sketch, "E191", {"start": v(99.25, 160) * mm, "end": v(99.25, 94.5) * mm});
            skLineSegment(sketch, "E192", {"start": v(99.25, 94.5) * mm, "end": v(0, 94.5) * mm});
            skLineSegment(sketch, "E193", {"start": v(85.07, 92.08) * mm, "end": v(85.07, 0) * mm});
            skLineSegment(sketch, "E194", {"start": v(99.75, 160) * mm, "end": v(99.75, 94) * mm});
            skLineSegment(sketch, "E195", {"start": v(99.75, 92.58) * mm, "end": v(220, 92.58) * mm});
            skLineSegment(sketch, "E196", {"start": v(220, 92.08) * mm, "end": v(85.07, 92.08) * mm});
            skLineSegment(sketch, "E197", {"start": v(99.75, 92.58) * mm, "end": v(85.07, 92.58) * mm});
            skLineSegment(sketch, "E198", {"start": v(85.07, 92.58) * mm, "end": v(85.07, 94) * mm});
            skLineSegment(sketch, "E199", {"start": v(85.07, 94) * mm, "end": v(99.75, 94) * mm});
            skLineSegment(sketch, "E200", {"start": v(0, 94) * mm, "end": v(32.31, 94) * mm});
            skLineSegment(sketch, "E201", {"start": v(84.57, 94) * mm, "end": v(84.57, 80.85) * mm});
            skLineSegment(sketch, "E202", {"start": v(84.57, 80.85) * mm, "end": v(32.81, 80.85) * mm});
            skLineSegment(sketch, "E203", {"start": v(0, 80.85) * mm, "end": v(0, 80.35) * mm, "construction": true});
            skLineSegment(sketch, "E204", {"start": v(0, 80.35) * mm, "end": v(32.31, 80.35) * mm});
            skLineSegment(sketch, "E205", {"start": v(32.31, 80.35) * mm, "end": v(32.31, 0) * mm});
            skLineSegment(sketch, "E206", {"start": v(32.31, 0) * mm, "end": v(32.81, 0) * mm});
            skLineSegment(sketch, "E207", {"start": v(32.81, 0) * mm, "end": v(32.81, 80.35) * mm});
            skLineSegment(sketch, "E208", {"start": v(32.81, 80.35) * mm, "end": v(84.57, 80.35) * mm});
            skLineSegment(sketch, "E209", {"start": v(84.57, 80.35) * mm, "end": v(84.57, 0) * mm});
            skLineSegment(sketch, "E210", {"start": v(84.57, 0) * mm, "end": v(85.07, 0) * mm});
            skPoint(sketch, "E211.orphan", {"position": v(220, 160) * mm});
            skPoint(sketch, "E212.orphan", {"position": v(220, 0) * mm});
            skPoint(sketch, "E213.orphan", {"position": v(0, 160) * mm});
            skLineSegment(sketch, "E214", {"start": v(99.75, 160) * mm, "end": v(99.25, 160) * mm});
            skLineSegment(sketch, "E215", {"start": v(85.07, 0) * mm, "end": v(84.57, 0) * mm});
            skLineSegment(sketch, "E216", {"start": v(32.81, 0) * mm, "end": v(32.31, 0) * mm});
            skPoint(sketch, "E217.orphan", {"position": v(0, 117.35) * mm});
            skLineSegment(sketch, "E218.trimOffspring", {"start": v(0, 80.85) * mm, "end": v(0, 80.35) * mm});
            skPoint(sketch, "E219.orphan", {"position": v(0, 43.35) * mm});
            skLineSegment(sketch, "E220.trimOffspring", {"start": v(84.57, 0) * mm, "end": v(219.64, 0) * mm});
            skPoint(sketch, "E221.0.start.orphan", {"position": v(-0.36, 0) * mm});
            skLineSegment(sketch, "E222", {"start": v(0, 80.85) * mm, "end": v(-2.19, 80.85) * mm});
            skLineSegment(sketch, "E223", {"start": v(-2.19, 80.85) * mm, "end": v(-2.19, 80.35) * mm});
            skLineSegment(sketch, "E224", {"start": v(-2.19, 80.35) * mm, "end": v(0, 80.35) * mm});
            skLineSegment(sketch, "E225", {"start": v(32.81, 80.85) * mm, "end": v(32.81, 94) * mm});
            skLineSegment(sketch, "E226", {"start": v(32.31, 80.85) * mm, "end": v(32.31, 94) * mm});
            skLineSegment(sketch, "E227.trimOffspring", {"start": v(32.31, 80.85) * mm, "end": v(0, 80.85) * mm});
            skLineSegment(sketch, "E228.trimOffspring", {"start": v(32.81, 94) * mm, "end": v(84.57, 94) * mm});
            skSolve(sketch);
        }
        {
            var Q0;
            Q0 = qSketchRegion(id + "F45", true);
            extrude(context, id + "F46", {"entities" : qUnion([Q0]), "operationType" : NewBodyOperationType.REMOVE, "endBound" : BoundingType.THROUGH_ALL, "oppositeDirection" : true, "depth" : 25 * mm});
        }
        {
            var Q0;
            Q0=makeQuery(id+"F3.opExtrude","CAP_FACE",FACE,{"disambiguationData":[OSD([sQuery(id+"F1.wireOp",EDGE,"E21"),sQuery(id+"F1.wireOp",EDGE,"E22"),sQuery(id+"F1.wireOp",EDGE,"E23"),sQuery(id+"F1.wireOp",EDGE,"E24")])],"isStart":false});
            var sketch = newSketch(context, id + "F47", { "sketchPlane" : qUnion([Q0])});
            skLineSegment(sketch, "E229", {"start": v(49, 92.58) * mm, "end": v(49, 97.58) * mm});
            skLineSegment(sketch, "E230", {"start": v(54, 92.58) * mm, "end": v(54, 97.58) * mm});
            skArc(sketch, "E231", {"start": v(54, 97.58) * mm, "mid": v(51.5, 100.08) * mm, "end": v(49, 97.58) * mm});
            skLineSegment(sketch, "E232", {"start": v(49, 92.58) * mm, "end": v(49.5, 92.58) * mm});
            skCircle(sketch, "E233.0", {"center": v(51.5, 124) * mm, "radius": 8 * mm, "construction": true});
            skLineSegment(sketch, "E234", {"start": v(49.5, 92.58) * mm, "end": v(49.5, 89.58) * mm});
            skLineSegment(sketch, "E235", {"start": v(53.5, 92.58) * mm, "end": v(53.5, 89.58) * mm});
            skArc(sketch, "E236", {"start": v(49.5, 89.58) * mm, "mid": v(51.5, 87.58) * mm, "end": v(53.5, 89.58) * mm});
            skLineSegment(sketch, "E237.trimOffspring", {"start": v(53.5, 92.58) * mm, "end": v(54, 92.58) * mm});
            skSolve(sketch);
        }
        {
            var Q0;
            Q0=makeQuery(id+"F47.imprint","IMPRINT",FACE,{"disambiguationData":[TD([[makeQuery(id+"F47.imprint","IMPRINT",EDGE,{"derivedFrom":sQuery(id+"F47.wireOp",EDGE,"E229")}),-1.0]])]});
            extrude(context, id + "F48", {"entities" : qUnion([Q0]), "operationType" : NewBodyOperationType.REMOVE, "oppositeDirection" : true, "depth" : 10 * mm});
        }
        {
            var Q0;
            {var subQ0=sQuery(id+"F1.wireOp",EDGE,"E22");var subQ1=sQuery(id+"F1.wireOp",EDGE,"E23");var subQ2=sQuery(id+"F1.wireOp",EDGE,"E24");Q0=makeQuery(id+"F46.boolean.opBoolean","SPLIT",FACE,{"disambiguationData":[TD([makeQuery(id+"F46.opExtrude","SWEPT_FACE",FACE,{"disambiguationData":[OSD([sQuery(id+"F45.wireOp",EDGE,"E196")])]})])],"derivedFrom":makeQuery(id+"F3.opExtrude","CAP_FACE",FACE,{"disambiguationData":[OSD([sQuery(id+"F1.wireOp",EDGE,"E21"),subQ0,subQ1,subQ2])],"isStart":false})});}
            cPlane(context, id + "F49", {"entities" : qUnion([Q0]), "cplaneType" : CPlaneType.OFFSET, "offset" : 26 * mm, "width" : 150 * mm, "height" : 150 * mm});
        }
        {
            var Q0;
            Q0=qCreatedBy(id+"F49.planeOp",FACE);
            var sketch = newSketch(context, id + "F50", { "sketchPlane" : qUnion([Q0])});
            skArc(sketch, "E238.0", {"start": v(49.5, 89.58) * mm, "mid": v(51.5, 87.58) * mm, "end": v(53.5, 89.58) * mm, "construction": true});
            skCircle(sketch, "E239", {"center": v(51.5, 89.58) * mm, "radius": 2 * mm});
            skSolve(sketch);
        }
        {
            var Q0;
            Q0=makeQuery(id+"F50.imprint","IMPRINT",FACE,{"disambiguationData":[TD([[makeQuery(id+"F50.imprint","IMPRINT",EDGE,{"derivedFrom":sQuery(id+"F50.wireOp",EDGE,"E239")}),1.0]])]});
            extrude(context, id + "F51", {"entities" : qUnion([Q0]), "oppositeDirection" : true, "depth" : 35 * mm});
        }
        {
            var Q0;
            Q0=makeQuery(id+"F51.opExtrude","CAP_FACE",FACE,{"disambiguationData":[OSD([sQuery(id+"F50.wireOp",EDGE,"E239")])],"isStart":true});
            cPlane(context, id + "F52", {"entities" : qUnion([Q0]), "cplaneType" : CPlaneType.OFFSET, "offset" : 2.5 * mm, "oppositeDirection" : true, "width" : 150 * mm, "height" : 150 * mm});
        }
        {
            var Q0;
            Q0=qCreatedBy(id+"F52.planeOp",FACE);
            var sketch = newSketch(context, id + "F53", { "sketchPlane" : qUnion([Q0])});
            skCircle(sketch, "E240.0", {"center": v(51.5, 89.58) * mm, "radius": 2 * mm, "construction": true});
            skCircle(sketch, "E241", {"center": v(51.5, 89.58) * mm, "radius": 2.75 * mm});
            skSolve(sketch);
        }
        {
            var Q0;
            Q0 = qSketchRegion(id + "F53", true);
            extrude(context, id + "F54", {"entities" : qUnion([Q0]), "operationType" : NewBodyOperationType.ADD, "oppositeDirection" : true, "depth" : 3 * mm});
        }
        {
            var Q0;
            Q0=qCreatedBy(makeId("Top.planeOp"),FACE);
            cPlane(context, id + "F55", {"entities" : qUnion([Q0]), "cplaneType" : CPlaneType.OFFSET, "offset" : 157 * mm, "width" : 150 * mm, "height" : 150 * mm});
        }
        {
            var Q0;
            Q0=qCreatedBy(id+"F55.planeOp",FACE);
            var sketch = newSketch(context, id + "F56", { "sketchPlane" : qUnion([Q0])});
            skCircle(sketch, "E242", {"center": v(107.12, 19.5) * mm, "radius": 5 * mm});
            skSolve(sketch);
        }
        {
            var Q0;
            Q0 = qSketchRegion(id + "F56", true);
            extrude(context, id + "F57", {"entities" : qUnion([Q0]), "oppositeDirection" : true, "depth" : 10 * mm});
        }
        {
            var Q0;
            Q0=makeQuery(id+"F23.opExtrude","CAP_EDGE",EDGE,{"disambiguationData":[OSD([sQuery(id+"F22.wireOp",EDGE,"E113")])],"isStart":false});
            fillet(context, id + "F58", {"entities" : qUnion([Q0]), "radius" : 5 * mm, "tangentPropagation" : true, "allowEdgeOverflow" : false});
        }
        {
            var Q0;
            Q0=qCreatedBy(id+"F55.planeOp",FACE);
            var Q1;
            Q1=sQuery(id+"F1.wireOp",EDGE,"E21");
            cPlane(context, id + "F59", {"entities" : qUnion([Q0, Q1]), "cplaneType" : CPlaneType.LINE_ANGLE, "offset" : 150 * mm, "angle" : 45 * degree, "width" : 150 * mm, "height" : 150 * mm});
        }
        {
            var Q0;
            Q0=qCreatedBy(id+"F59.planeOp",FACE);
            var sketch = newSketch(context, id + "F60", { "sketchPlane" : qUnion([Q0])});
            skCircle(sketch, "E243", {"center": v(200, -112.7) * mm, "radius": 9 * mm});
            skLineSegment(sketch, "E244.0", {"start": v(200, -121.28) * mm, "end": v(200, -112.7) * mm, "construction": true});
            skLineSegment(sketch, "E245", {"start": v(242, -125.32) * mm, "end": v(200, -125.32) * mm, "construction": true});
            skSolve(sketch);
        }
        {
            var Q0;
            Q0 = qSketchRegion(id + "F60", true);
            extrude(context, id + "F61", {"entities" : qUnion([Q0]), "oppositeDirection" : true, "depth" : 50 * mm});
        }
        {
            var Q0;
            Q0=makeQuery(id+"F61.opExtrude","CAP_EDGE",EDGE,{"disambiguationData":[OSD([sQuery(id+"F60.wireOp",EDGE,"E243")])],"isStart":false});
            chamfer(context, id + "F62", {"entities" : qUnion([Q0]), "width" : 2 * mm, "tangentPropagation" : true});
        }
        {
            var Q0;
            Q0=qCreatedBy(makeId("Top.planeOp"),FACE);
            var sketch = newSketch(context, id + "F63", { "sketchPlane" : qUnion([Q0])});
            skLineSegment(sketch, "E246.0", {"start": v(217, 29.5) * mm, "end": v(205, 29.5) * mm});
            skLineSegment(sketch, "E246.1", {"start": v(205, 43) * mm, "end": v(205, 29.07) * mm});
            skLineSegment(sketch, "E247.bottom", {"start": v(205, 29.5) * mm, "end": v(211.48, 29.5) * mm});
            skLineSegment(sketch, "E247.top", {"start": v(205, 35.84) * mm, "end": v(211.48, 35.84) * mm});
            skLineSegment(sketch, "E247.left", {"start": v(205, 29.5) * mm, "end": v(205, 35.84) * mm});
            skLineSegment(sketch, "E247.right", {"start": v(211.48, 29.5) * mm, "end": v(211.48, 35.84) * mm});
            skSolve(sketch);
        }
        {
            var Q0;
            Q0 = qSketchRegion(id + "F63", true);
            extrude(context, id + "F64", {"entities" : qUnion([Q0]), "operationType" : NewBodyOperationType.REMOVE, "endBound" : BoundingType.THROUGH_ALL, "depth" : 25 * mm});
        }
        {
            var Q0;
            Q0=qCreatedBy(id+"F18.planeOp",FACE);
            var sketch = newSketch(context, id + "F65", { "sketchPlane" : qUnion([Q0])});
            skLineSegment(sketch, "E248.bottom", {"start": v(22.03, 65.37) * mm, "end": v(210.7, 65.37) * mm});
            skLineSegment(sketch, "E248.top", {"start": v(22.03, 15.17) * mm, "end": v(210.7, 15.17) * mm});
            skLineSegment(sketch, "E248.left", {"start": v(22.03, 65.37) * mm, "end": v(22.03, 15.17) * mm});
            skLineSegment(sketch, "E248.right", {"start": v(210.7, 65.37) * mm, "end": v(210.7, 15.17) * mm});
            skSolve(sketch);
        }
        {
            var Q0;
            Q0 = qSketchRegion(id + "F65", true);
            extrude(context, id + "F66", {"entities" : qUnion([Q0]), "operationType" : NewBodyOperationType.ADD, "oppositeDirection" : true, "depth" : 50 * mm});
        }
        {
            var Q0;
            Q0=makeQuery(id+"F46.boolean.opBoolean","SPLIT",FACE,{"disambiguationData":[TD([makeQuery(id+"F46.opExtrude","SWEPT_FACE",FACE,{"disambiguationData":[OSD([sQuery(id+"F45.wireOp",EDGE,"E207")])]})])],"derivedFrom":makeQuery(id+"F3.opExtrude","SWEPT_FACE",FACE,{"disambiguationData":[OSD([sQuery(id+"F1.wireOp",EDGE,"E24")])]})});
            var sketch = newSketch(context, id + "F67", { "sketchPlane" : qUnion([Q0])});
            skCircle(sketch, "E249", {"center": v(-68.12, 62.83) * mm, "radius": 7.54 * mm});
            skCircle(sketch, "E250", {"center": v(-68.12, 62.83) * mm, "radius": 7.04 * mm});
            skSolve(sketch);
        }
        {
            var Q0;
            Q0 = qSketchRegion(id + "F67", true);
            extrude(context, id + "F68", {"entities" : qUnion([Q0]), "operationType" : NewBodyOperationType.REMOVE, "oppositeDirection" : true, "depth" : 5 * mm});
        }
        {
            var Q0;
            Q0=makeQuery(id+"F44.opExtrude","CAP_FACE",FACE,{"disambiguationData":[OSD([sQuery(id+"F43.wireOp",EDGE,"E177"),sQuery(id+"F43.wireOp",EDGE,"E178"),sQuery(id+"F43.wireOp",EDGE,"E179"),sQuery(id+"F43.wireOp",EDGE,"E185.trimOffspring")])],"isStart":false});
            var sketch = newSketch(context, id + "F69", { "sketchPlane" : qUnion([Q0])});
            skCircle(sketch, "E251", {"center": v(51.5, 150.27) * mm, "radius": 3.5 * mm});
            skArc(sketch, "E252.0", {"start": v(81, 123.35) * mm, "mid": v(79.83, 126.17) * mm, "end": v(77, 127.35) * mm, "construction": true});
            skCircle(sketch, "E253", {"center": v(77, 123.35) * mm, "radius": 3.5 * mm});
            skSolve(sketch);
        }
        {
            var Q0;
            Q0 = qSketchRegion(id + "F69", true);
            extrude(context, id + "F70", {"entities" : qUnion([Q0]), "operationType" : NewBodyOperationType.ADD, "depth" : 2 * mm});
        }
        {
            var Q0;
            Q0=makeQuery(id+"F20.boolean.opBoolean","COPY",FACE,{"derivedFrom":makeQuery(id+"F20.opExtrude","CAP_FACE",FACE,{"disambiguationData":[OSD([sQuery(id+"F19.wireOp",EDGE,"E93"),sQuery(id+"F19.wireOp",EDGE,"E94"),sQuery(id+"F19.wireOp",EDGE,"E102"),sQuery(id+"F19.wireOp",EDGE,"E103"),sQuery(id+"F19.wireOp",EDGE,"E104")])],"isStart":true})});
            var sketch = newSketch(context, id + "F71", { "sketchPlane" : qUnion([Q0])});
            skCircle(sketch, "E254", {"center": v(5.07, 78.55) * mm, "radius": 4.5 * mm});
            skCircle(sketch, "E255", {"center": v(90.25, 79.73) * mm, "radius": 4.5 * mm});
            skCircle(sketch, "E256", {"center": v(90.2, 4.9) * mm, "radius": 4.5 * mm});
            skArc(sketch, "E257.0", {"start": v(95.57, 4.9) * mm, "mid": v(90.2, 10.28) * mm, "end": v(84.82, 4.9) * mm, "construction": true});
            skArc(sketch, "E258.0", {"start": v(84.87, 79.73) * mm, "mid": v(90.25, 74.36) * mm, "end": v(95.62, 79.73) * mm, "construction": true});
            skSolve(sketch);
        }
        {
            var Q0;
            Q0 = qSketchRegion(id + "F71", true);
            extrude(context, id + "F72", {"entities" : qUnion([Q0]), "operationType" : NewBodyOperationType.ADD, "depth" : 3 * mm});
        }
        {
            var Q0;
            Q0=makeQuery(id+"F57.opExtrude","CAP_FACE",FACE,{"disambiguationData":[OSD([sQuery(id+"F56.wireOp",EDGE,"E242")])],"isStart":true});
            var sketch = newSketch(context, id + "F73", { "sketchPlane" : qUnion([Q0])});
            skCircle(sketch, "E259", {"center": v(107.12, 19.5) * mm, "radius": 4.5 * mm});
            skSolve(sketch);
        }
        {
            var Q0;
            Q0 = qSketchRegion(id + "F73", true);
            extrude(context, id + "F74", {"entities" : qUnion([Q0]), "operationType" : NewBodyOperationType.ADD, "depth" : 3 * mm});
        }
        {
            var Q0;
            {var subQ0=sQuery(id+"F4.wireOp",EDGE,"E54");var subQ1=sQuery(id+"F1.wireOp",EDGE,"E21");Q0=makeQuery(id+"F7.boolean.opBoolean","SPLIT",FACE,{"disambiguationData":[TD([makeQuery(id+"F3.opExtrude","SWEPT_FACE",FACE,{"disambiguationData":[OSD([subQ1])]})])],"derivedFrom":makeQuery(id+"F5.boolean.opBoolean","COPY",FACE,{"derivedFrom":makeQuery(id+"F5.opExtrude","SWEPT_FACE",FACE,{"disambiguationData":[OSD([subQ0])]})})});}
            var sketch = newSketch(context, id + "F75", { "sketchPlane" : qUnion([Q0])});
            skCircle(sketch, "E260", {"center": v(215, 81) * mm, "radius": 4.5 * mm});
            skSolve(sketch);
        }
        {
            var Q0;
            Q0 = qSketchRegion(id + "F75", true);
            extrude(context, id + "F76", {"entities" : qUnion([Q0]), "operationType" : NewBodyOperationType.ADD, "depth" : 3 * mm});
        }
        {
            var Q0;
            Q0=makeQuery(id+"F5.boolean.opBoolean","COPY",FACE,{"derivedFrom":makeQuery(id+"F5.opExtrude","SWEPT_FACE",FACE,{"disambiguationData":[OSD([sQuery(id+"F4.wireOp",EDGE,"E56")])]})});
            var sketch = newSketch(context, id + "F77", { "sketchPlane" : qUnion([Q0])});
            skCircle(sketch, "E261", {"center": v(214.77, 8.3) * mm, "radius": 4.5 * mm});
            skSolve(sketch);
        }
        {
            var Q0;
            Q0 = qSketchRegion(id + "F77", true);
            extrude(context, id + "F78", {"entities" : qUnion([Q0]), "operationType" : NewBodyOperationType.ADD, "depth" : 3 * mm});
        }
        {
            var Q0;
            Q0=makeQuery(id+"F70.opExtrude","CAP_EDGE",EDGE,{"disambiguationData":[OSD([sQuery(id+"F69.wireOp",EDGE,"E251")])],"isStart":false});
            var Q1;
            Q1=makeQuery(id+"F70.opExtrude","CAP_EDGE",EDGE,{"disambiguationData":[OSD([sQuery(id+"F69.wireOp",EDGE,"E253")])],"isStart":false});
            var Q2;
            Q2=makeQuery(id+"F74.opExtrude","CAP_EDGE",EDGE,{"disambiguationData":[OSD([sQuery(id+"F73.wireOp",EDGE,"E259")])],"isStart":false});
            var Q3;
            Q3=makeQuery(id+"F72.opExtrude","CAP_EDGE",EDGE,{"disambiguationData":[OSD([sQuery(id+"F71.wireOp",EDGE,"E255")])],"isStart":false});
            var Q4;
            Q4=makeQuery(id+"F72.opExtrude","CAP_EDGE",EDGE,{"disambiguationData":[OSD([sQuery(id+"F71.wireOp",EDGE,"E254")])],"isStart":false});
            var Q5;
            Q5=makeQuery(id+"F76.opExtrude","CAP_EDGE",EDGE,{"disambiguationData":[OSD([sQuery(id+"F75.wireOp",EDGE,"E260")])],"isStart":false});
            var Q6;
            Q6=makeQuery(id+"F78.opExtrude","CAP_EDGE",EDGE,{"disambiguationData":[OSD([sQuery(id+"F77.wireOp",EDGE,"E261")])],"isStart":false});
            fillet(context, id + "F79", {"entities" : qUnion([Q0, Q1, Q2, Q3, Q4, Q5, Q6]), "radius" : 1 * mm, "tangentPropagation" : true, "allowEdgeOverflow" : false});
        }
        {
            var Q0;
            Q0=makeQuery(id+"F70.opExtrude","CAP_FACE",FACE,{"disambiguationData":[OSD([sQuery(id+"F69.wireOp",EDGE,"E251")])],"isStart":false});
            var sketch = newSketch(context, id + "F80", { "sketchPlane" : qUnion([Q0])});
            skArc(sketch, "E262.0", {"start": v(48.04, 150.77) * mm, "mid": v(48, 150.27) * mm, "end": v(48.04, 149.77) * mm});
            skLineSegment(sketch, "E263", {"start": v(51, 153.73) * mm, "end": v(51, 150.77) * mm});
            skLineSegment(sketch, "E264", {"start": v(52, 153.73) * mm, "end": v(52, 150.77) * mm});
            skLineSegment(sketch, "E265", {"start": v(48.04, 150.77) * mm, "end": v(51, 150.77) * mm});
            skLineSegment(sketch, "E266", {"start": v(48.04, 149.77) * mm, "end": v(51, 149.77) * mm});
            skLineSegment(sketch, "E267.trimOffspring", {"start": v(52, 150.77) * mm, "end": v(54.96, 150.77) * mm});
            skLineSegment(sketch, "E268.trimOffspring", {"start": v(51, 149.77) * mm, "end": v(51, 146.8) * mm});
            skLineSegment(sketch, "E269.trimOffspring", {"start": v(52, 149.77) * mm, "end": v(54.96, 149.77) * mm});
            skLineSegment(sketch, "E270.trimOffspring", {"start": v(52, 149.77) * mm, "end": v(52, 146.8) * mm});
            skArc(sketch, "E271.trimOffspring", {"start": v(51, 146.8) * mm, "mid": v(51.5, 146.77) * mm, "end": v(52, 146.8) * mm});
            skArc(sketch, "E272.trimOffspring", {"start": v(54.96, 149.77) * mm, "mid": v(55, 150.27) * mm, "end": v(54.96, 150.77) * mm});
            skArc(sketch, "E273.trimOffspring", {"start": v(52, 153.73) * mm, "mid": v(51.5, 153.77) * mm, "end": v(51, 153.73) * mm});
            skLineSegment(sketch, "E274", {"start": v(73.54, 122.85) * mm, "end": v(76.5, 122.85) * mm});
            skLineSegment(sketch, "E275.trimOffspring", {"start": v(77.5, 123.85) * mm, "end": v(80.46, 123.85) * mm});
            skLineSegment(sketch, "E276", {"start": v(77.5, 126.8) * mm, "end": v(77.5, 123.85) * mm});
            skLineSegment(sketch, "E277.trimOffspring", {"start": v(76.5, 122.85) * mm, "end": v(76.5, 119.88) * mm});
            skLineSegment(sketch, "E278.trimOffspring", {"start": v(77.5, 122.85) * mm, "end": v(77.5, 119.88) * mm});
            skLineSegment(sketch, "E279.trimOffspring", {"start": v(77.5, 122.85) * mm, "end": v(80.46, 122.85) * mm});
            skLineSegment(sketch, "E280", {"start": v(73.54, 123.85) * mm, "end": v(76.5, 123.85) * mm});
            skLineSegment(sketch, "E281", {"start": v(76.5, 126.8) * mm, "end": v(76.5, 123.85) * mm});
            skArc(sketch, "E282.trimOffspring", {"start": v(77.5, 126.8) * mm, "mid": v(77, 126.85) * mm, "end": v(76.5, 126.8) * mm});
            skArc(sketch, "E283.trimOffspring", {"start": v(76.5, 119.88) * mm, "mid": v(77, 119.85) * mm, "end": v(77.5, 119.88) * mm});
            skArc(sketch, "E284.0", {"start": v(73.54, 123.85) * mm, "mid": v(73.5, 123.35) * mm, "end": v(73.54, 122.85) * mm});
            skArc(sketch, "E285.trimOffspring", {"start": v(80.46, 122.85) * mm, "mid": v(80.5, 123.35) * mm, "end": v(80.46, 123.85) * mm});
            skCircle(sketch, "E286.0", {"center": v(77, 123.35) * mm, "radius": 3.5 * mm, "construction": true});
            skSolve(sketch);
        }
        {
            var Q0;
            Q0 = qSketchRegion(id + "F80", true);
            extrude(context, id + "F81", {"entities" : qUnion([Q0]), "operationType" : NewBodyOperationType.REMOVE, "oppositeDirection" : true, "depth" : 1 * mm});
        }
        {
            var Q0;
            Q0=makeQuery(id+"F72.opExtrude","CAP_FACE",FACE,{"disambiguationData":[OSD([sQuery(id+"F71.wireOp",EDGE,"E254")])],"isStart":false});
            var sketch = newSketch(context, id + "F82", { "sketchPlane" : qUnion([Q0])});
            skLineSegment(sketch, "E287", {"start": v(0.63, 77.8) * mm, "end": v(4.32, 77.8) * mm});
            skLineSegment(sketch, "E288.trimOffspring", {"start": v(5.82, 79.3) * mm, "end": v(9.5, 79.3) * mm});
            skLineSegment(sketch, "E289", {"start": v(5.82, 82.99) * mm, "end": v(5.82, 79.3) * mm});
            skLineSegment(sketch, "E290.trimOffspring", {"start": v(4.32, 77.8) * mm, "end": v(4.32, 74.11) * mm});
            skLineSegment(sketch, "E291.trimOffspring", {"start": v(5.82, 77.8) * mm, "end": v(5.82, 74.11) * mm});
            skLineSegment(sketch, "E292.trimOffspring", {"start": v(5.82, 77.8) * mm, "end": v(9.5, 77.8) * mm});
            skLineSegment(sketch, "E293", {"start": v(0.63, 79.3) * mm, "end": v(4.32, 79.3) * mm});
            skLineSegment(sketch, "E294", {"start": v(4.32, 82.99) * mm, "end": v(4.32, 79.3) * mm});
            skArc(sketch, "E295.trimOffspring", {"start": v(5.82, 82.99) * mm, "mid": v(5.07, 83.05) * mm, "end": v(4.32, 82.99) * mm});
            skArc(sketch, "E296.trimOffspring", {"start": v(4.32, 74.11) * mm, "mid": v(5.07, 74.05) * mm, "end": v(5.82, 74.11) * mm});
            skArc(sketch, "E297.0", {"start": v(0.63, 79.3) * mm, "mid": v(0.57, 78.55) * mm, "end": v(0.63, 77.8) * mm});
            skArc(sketch, "E298.trimOffspring", {"start": v(9.5, 77.8) * mm, "mid": v(9.57, 78.55) * mm, "end": v(9.5, 79.3) * mm});
            skCircle(sketch, "E299.0", {"center": v(5.07, 78.55) * mm, "radius": 4.5 * mm, "construction": true});
            skLineSegment(sketch, "E300.trimOffspring", {"start": v(91, 80.48) * mm, "end": v(94.9, 80.48) * mm});
            skLineSegment(sketch, "E301.trimOffspring", {"start": v(91, 78.98) * mm, "end": v(91, 75.07) * mm});
            skLineSegment(sketch, "E302.trimOffspring", {"start": v(89.5, 78.98) * mm, "end": v(89.5, 75.07) * mm});
            skLineSegment(sketch, "E303", {"start": v(85.58, 80.48) * mm, "end": v(89.5, 80.48) * mm});
            skLineSegment(sketch, "E304.trimOffspring", {"start": v(91, 78.98) * mm, "end": v(94.9, 78.98) * mm});
            skLineSegment(sketch, "E305", {"start": v(85.58, 78.98) * mm, "end": v(89.5, 78.98) * mm});
            skCircle(sketch, "E306.0", {"center": v(90.25, 79.73) * mm, "radius": 4.72 * mm, "construction": true});
            skLineSegment(sketch, "E307", {"start": v(89.5, 84.4) * mm, "end": v(89.5, 80.48) * mm});
            skLineSegment(sketch, "E308", {"start": v(91, 84.4) * mm, "end": v(91, 80.48) * mm});
            skArc(sketch, "E309.trimOffspring", {"start": v(94.9, 78.98) * mm, "mid": v(94.97, 79.73) * mm, "end": v(94.9, 80.48) * mm});
            skArc(sketch, "E310.trimOffspring", {"start": v(91, 84.4) * mm, "mid": v(90.25, 84.46) * mm, "end": v(89.5, 84.4) * mm});
            skArc(sketch, "E311.0", {"start": v(85.58, 80.48) * mm, "mid": v(85.52, 79.73) * mm, "end": v(85.58, 78.98) * mm});
            skArc(sketch, "E312.trimOffspring", {"start": v(89.5, 75.07) * mm, "mid": v(90.25, 75.01) * mm, "end": v(91, 75.07) * mm});
            skLineSegment(sketch, "E313.trimOffspring", {"start": v(90.95, 5.66) * mm, "end": v(94.64, 5.66) * mm});
            skLineSegment(sketch, "E314.trimOffspring", {"start": v(90.95, 4.16) * mm, "end": v(90.95, 0.47) * mm});
            skLineSegment(sketch, "E315.trimOffspring", {"start": v(89.45, 4.16) * mm, "end": v(89.45, 0.47) * mm});
            skLineSegment(sketch, "E316", {"start": v(85.76, 5.66) * mm, "end": v(89.45, 5.66) * mm});
            skLineSegment(sketch, "E317.trimOffspring", {"start": v(90.95, 4.16) * mm, "end": v(94.64, 4.16) * mm});
            skLineSegment(sketch, "E318", {"start": v(85.76, 4.16) * mm, "end": v(89.45, 4.16) * mm});
            skCircle(sketch, "E319.0", {"center": v(90.2, 4.9) * mm, "radius": 4.5 * mm, "construction": true});
            skLineSegment(sketch, "E320", {"start": v(89.45, 9.34) * mm, "end": v(89.45, 5.66) * mm});
            skLineSegment(sketch, "E321", {"start": v(90.95, 9.34) * mm, "end": v(90.95, 5.66) * mm});
            skArc(sketch, "E322.trimOffspring", {"start": v(94.64, 4.16) * mm, "mid": v(94.7, 4.9) * mm, "end": v(94.64, 5.66) * mm});
            skArc(sketch, "E323.trimOffspring", {"start": v(90.95, 9.34) * mm, "mid": v(90.2, 9.4) * mm, "end": v(89.45, 9.34) * mm});
            skArc(sketch, "E324.0", {"start": v(85.76, 5.66) * mm, "mid": v(85.7, 4.9) * mm, "end": v(85.76, 4.16) * mm});
            skArc(sketch, "E325.trimOffspring", {"start": v(89.45, 0.47) * mm, "mid": v(90.2, 0.4) * mm, "end": v(90.95, 0.47) * mm});
            skCircle(sketch, "E326.0", {"center": v(90.25, 79.73) * mm, "radius": 3.5 * mm, "construction": true});
            skCircle(sketch, "E327.0", {"center": v(90.25, 79.73) * mm, "radius": 4.5 * mm, "construction": true});
            skSolve(sketch);
        }
        {
            var Q0;
            Q0 = qSketchRegion(id + "F82", true);
            extrude(context, id + "F83", {"entities" : qUnion([Q0]), "operationType" : NewBodyOperationType.REMOVE, "oppositeDirection" : true, "depth" : 1 * mm});
        }
        {
            var Q0;
            Q0=makeQuery(id+"F74.opExtrude","CAP_FACE",FACE,{"disambiguationData":[OSD([sQuery(id+"F73.wireOp",EDGE,"E259")])],"isStart":false});
            var sketch = newSketch(context, id + "F84", { "sketchPlane" : qUnion([Q0])});
            skCircle(sketch, "E328.0", {"center": v(107.12, 19.5) * mm, "radius": 4.5 * mm, "construction": true});
            skArc(sketch, "E329.trimOffspring", {"start": v(107.87, 23.94) * mm, "mid": v(107.12, 24) * mm, "end": v(106.37, 23.94) * mm});
            skLineSegment(sketch, "E330", {"start": v(106.37, 23.94) * mm, "end": v(106.37, 20.25) * mm});
            skArc(sketch, "E331.trimOffspring", {"start": v(111.56, 18.75) * mm, "mid": v(111.62, 19.5) * mm, "end": v(111.56, 20.25) * mm});
            skLineSegment(sketch, "E332.trimOffspring", {"start": v(107.87, 18.75) * mm, "end": v(111.56, 18.75) * mm});
            skLineSegment(sketch, "E333", {"start": v(102.68, 20.25) * mm, "end": v(106.37, 20.25) * mm});
            skLineSegment(sketch, "E334.trimOffspring", {"start": v(106.37, 18.75) * mm, "end": v(106.37, 15.07) * mm});
            skLineSegment(sketch, "E335.trimOffspring", {"start": v(107.87, 18.75) * mm, "end": v(107.87, 15.07) * mm});
            skArc(sketch, "E336.0", {"start": v(102.68, 20.25) * mm, "mid": v(102.62, 19.5) * mm, "end": v(102.68, 18.75) * mm});
            skLineSegment(sketch, "E337.trimOffspring", {"start": v(107.87, 20.25) * mm, "end": v(111.56, 20.25) * mm});
            skLineSegment(sketch, "E338", {"start": v(107.87, 23.94) * mm, "end": v(107.87, 20.25) * mm});
            skLineSegment(sketch, "E339", {"start": v(102.68, 18.75) * mm, "end": v(106.37, 18.75) * mm});
            skArc(sketch, "E340.trimOffspring", {"start": v(106.37, 15.07) * mm, "mid": v(107.12, 15) * mm, "end": v(107.87, 15.07) * mm});
            skSolve(sketch);
        }
        {
            var Q0;
            Q0 = qSketchRegion(id + "F84", true);
            extrude(context, id + "F85", {"entities" : qUnion([Q0]), "operationType" : NewBodyOperationType.REMOVE, "oppositeDirection" : true, "depth" : 1 * mm});
        }
        {
            var Q0;
            Q0=makeQuery(id+"F25.boolean.opBoolean","COPY",FACE,{"derivedFrom":makeQuery(id+"F25.opExtrude","CAP_FACE",FACE,{"disambiguationData":[OSD([sQuery(id+"F24.wireOp",EDGE,"E119"),sQuery(id+"F24.wireOp",EDGE,"E120"),sQuery(id+"F24.wireOp",EDGE,"E121"),sQuery(id+"F24.wireOp",EDGE,"E123.MirrorCS"),sQuery(id+"F24.wireOp",EDGE,"E124.MirrorCS"),sQuery(id+"F24.wireOp",EDGE,"E125.MirrorCS"),sQuery(id+"F24.wireOp",EDGE,"E127.0"),sQuery(id+"F24.wireOp",EDGE,"E128.0"),sQuery(id+"F24.wireOp",EDGE,"E129.0"),sQuery(id+"F24.wireOp",EDGE,"E130.0"),sQuery(id+"F24.wireOp",EDGE,"E131.0"),sQuery(id+"F24.wireOp",EDGE,"E132.trimOffspring"),sQuery(id+"F24.wireOp",EDGE,"E133")])],"isStart":false})});
            var sketch = newSketch(context, id + "F86", { "sketchPlane" : qUnion([Q0])});
            skCircle(sketch, "E341", {"center": v(-65.64, 6.48) * mm, "radius": 4 * mm});
            skLineSegment(sketch, "E342", {"start": v(-43, 0) * mm, "end": v(-43, 14.87) * mm, "construction": true});
            skCircle(sketch, "E343.MirrorC", {"center": v(-20.36, 6.48) * mm, "radius": 4 * mm});
            skSolve(sketch);
        }
        {
            var Q0;
            Q0 = qSketchRegion(id + "F86", true);
            extrude(context, id + "F87", {"entities" : qUnion([Q0]), "operationType" : NewBodyOperationType.REMOVE, "oppositeDirection" : true, "depth" : 3 * mm});
        }
        {
            var Q0;
            Q0=makeQuery(id+"F76.opExtrude","CAP_FACE",FACE,{"disambiguationData":[OSD([sQuery(id+"F75.wireOp",EDGE,"E260")])],"isStart":false});
            var sketch = newSketch(context, id + "F88", { "sketchPlane" : qUnion([Q0])});
            skLineSegment(sketch, "E344.trimOffspring", {"start": v(215.75, 81.75) * mm, "end": v(219.44, 81.75) * mm});
            skLineSegment(sketch, "E345", {"start": v(210.56, 80.25) * mm, "end": v(214.25, 80.25) * mm});
            skLineSegment(sketch, "E346.trimOffspring", {"start": v(214.25, 80.25) * mm, "end": v(214.25, 76.56) * mm});
            skLineSegment(sketch, "E347", {"start": v(215.75, 85.44) * mm, "end": v(215.75, 81.75) * mm});
            skLineSegment(sketch, "E348.trimOffspring", {"start": v(215.75, 80.25) * mm, "end": v(219.44, 80.25) * mm});
            skLineSegment(sketch, "E349.trimOffspring", {"start": v(215.75, 80.25) * mm, "end": v(215.75, 76.56) * mm});
            skLineSegment(sketch, "E350", {"start": v(210.56, 81.75) * mm, "end": v(214.25, 81.75) * mm});
            skLineSegment(sketch, "E351", {"start": v(214.25, 85.44) * mm, "end": v(214.25, 81.75) * mm});
            skCircle(sketch, "E352.0", {"center": v(215, 81) * mm, "radius": 4.5 * mm, "construction": true});
            skArc(sketch, "E353.trimOffspring", {"start": v(214.25, 76.56) * mm, "mid": v(215, 76.5) * mm, "end": v(215.75, 76.56) * mm});
            skArc(sketch, "E354.trimOffspring", {"start": v(215.75, 85.44) * mm, "mid": v(215, 85.5) * mm, "end": v(214.25, 85.44) * mm});
            skArc(sketch, "E355.trimOffspring", {"start": v(219.44, 80.25) * mm, "mid": v(219.5, 81) * mm, "end": v(219.44, 81.75) * mm});
            skArc(sketch, "E356.0", {"start": v(210.56, 81.75) * mm, "mid": v(210.5, 81) * mm, "end": v(210.56, 80.25) * mm});
            skSolve(sketch);
        }
        {
            var Q0;
            Q0 = qSketchRegion(id + "F88", true);
            extrude(context, id + "F89", {"entities" : qUnion([Q0]), "operationType" : NewBodyOperationType.REMOVE, "oppositeDirection" : true, "depth" : 1 * mm});
        }
        {
            var Q0;
            Q0=makeQuery(id+"F78.opExtrude","CAP_FACE",FACE,{"disambiguationData":[OSD([sQuery(id+"F77.wireOp",EDGE,"E261")])],"isStart":false});
            var sketch = newSketch(context, id + "F90", { "sketchPlane" : qUnion([Q0])});
            skLineSegment(sketch, "E357.trimOffspring", {"start": v(215.52, 9.06) * mm, "end": v(219.2, 9.06) * mm});
            skLineSegment(sketch, "E358", {"start": v(210.34, 7.56) * mm, "end": v(214.02, 7.56) * mm});
            skLineSegment(sketch, "E359.trimOffspring", {"start": v(214.02, 7.56) * mm, "end": v(214.02, 3.87) * mm});
            skLineSegment(sketch, "E360", {"start": v(215.52, 12.74) * mm, "end": v(215.52, 9.06) * mm});
            skLineSegment(sketch, "E361.trimOffspring", {"start": v(215.52, 7.56) * mm, "end": v(219.2, 7.56) * mm});
            skLineSegment(sketch, "E362.trimOffspring", {"start": v(215.52, 7.56) * mm, "end": v(215.52, 3.87) * mm});
            skLineSegment(sketch, "E363", {"start": v(210.34, 9.06) * mm, "end": v(214.02, 9.06) * mm});
            skLineSegment(sketch, "E364", {"start": v(214.02, 12.74) * mm, "end": v(214.02, 9.06) * mm});
            skCircle(sketch, "E365.0", {"center": v(214.77, 8.3) * mm, "radius": 4.5 * mm, "construction": true});
            skArc(sketch, "E366.trimOffspring", {"start": v(214.02, 3.87) * mm, "mid": v(214.77, 3.8) * mm, "end": v(215.52, 3.87) * mm});
            skArc(sketch, "E367.trimOffspring", {"start": v(215.52, 12.74) * mm, "mid": v(214.77, 12.8) * mm, "end": v(214.02, 12.74) * mm});
            skArc(sketch, "E368.trimOffspring", {"start": v(219.2, 7.56) * mm, "mid": v(219.27, 8.3) * mm, "end": v(219.2, 9.06) * mm});
            skArc(sketch, "E369.0", {"start": v(210.34, 9.06) * mm, "mid": v(210.27, 8.3) * mm, "end": v(210.34, 7.56) * mm});
            skSolve(sketch);
        }
        {
            var Q0;
            Q0 = qSketchRegion(id + "F90", true);
            extrude(context, id + "F91", {"entities" : qUnion([Q0]), "operationType" : NewBodyOperationType.REMOVE, "oppositeDirection" : true, "depth" : 1 * mm});
        }
    });
